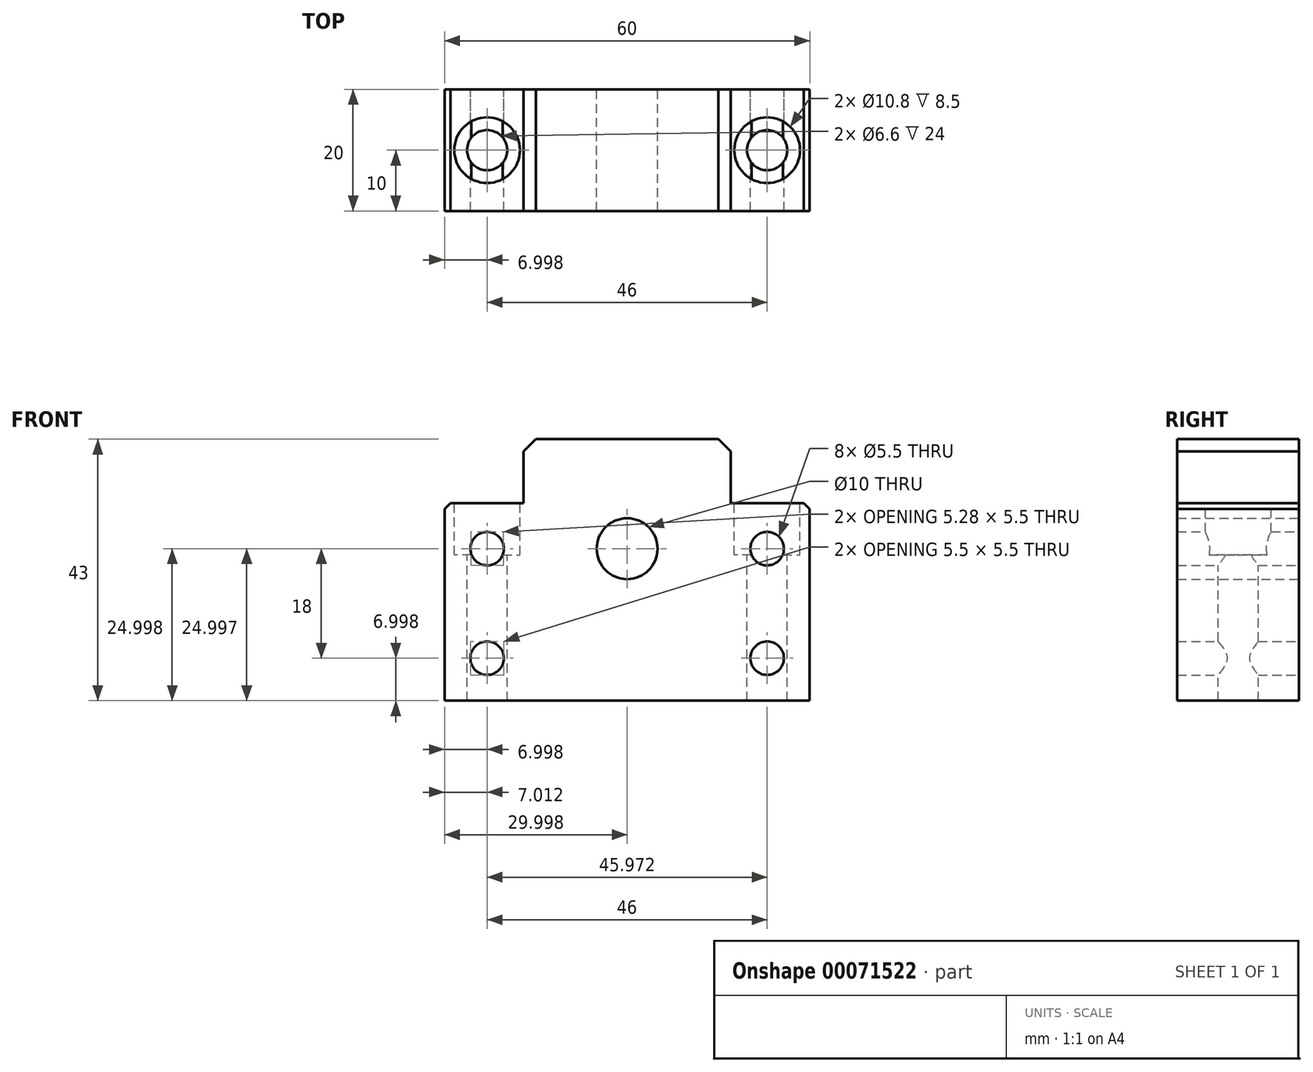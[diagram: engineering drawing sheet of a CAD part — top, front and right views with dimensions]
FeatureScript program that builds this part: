
annotation { "Feature Type Name" : "Feature", "Feature Type Description" : "" }
export const myFeature = defineFeature(function(context is Context, id is Id, definition is map)
    precondition{}
    {
        {
            var Q0;
            Q0=qCreatedBy(makeId("Front.planeOp"),FACE);
            var sketch = newSketch(context, id + "F0", { "sketchPlane" : qUnion([Q0])});
            skLineSegment(sketch, "E0.bottom", {"start": v(-44.44, 5.92) * mm, "end": v(-31.44, 5.92) * mm});
            skLineSegment(sketch, "E0.top", {"start": v(-44.44, -26.58) * mm, "end": v(15.56, -26.58) * mm});
            skLineSegment(sketch, "E0.left", {"start": v(-44.44, 5.92) * mm, "end": v(-44.44, -26.58) * mm});
            skLineSegment(sketch, "E0.right", {"start": v(15.56, 5.92) * mm, "end": v(15.56, -26.58) * mm});
            skLineSegment(sketch, "E1.bottom", {"start": v(-31.44, 16.42) * mm, "end": v(2.56, 16.42) * mm});
            skLineSegment(sketch, "E1.left", {"start": v(-31.44, 16.42) * mm, "end": v(-31.44, 5.92) * mm});
            skLineSegment(sketch, "E1.right", {"start": v(2.56, 16.42) * mm, "end": v(2.56, 5.92) * mm});
            skLineSegment(sketch, "E2.trimOffspring", {"start": v(2.56, 5.92) * mm, "end": v(15.56, 5.92) * mm});
            skCircle(sketch, "E3", {"center": v(-14.44, -1.58) * mm, "radius": 5 * mm});
            skCircle(sketch, "E4", {"center": v(-37.44, -1.58) * mm, "radius": 2.75 * mm});
            skCircle(sketch, "E5", {"center": v(-37.44, -19.58) * mm, "radius": 2.75 * mm});
            skCircle(sketch, "E6", {"center": v(8.56, -19.58) * mm, "radius": 2.75 * mm});
            skCircle(sketch, "E7", {"center": v(8.56, -1.58) * mm, "radius": 2.75 * mm});
            skSolve(sketch);
        }
        {
            var Q0;
            Q0=qSketchRegion(id+"F0",true);
            extrude(context, id + "F1", {"entities" : qUnion([Q0]), "depth" : 20 * mm});
        }
        {
            var Q0;
            Q0=makeQuery(id+"F1.opExtrude","SWEPT_EDGE",EDGE,{"disambiguationData":[OSD([sQuery(id+"F0.wireOp",EDGE,"E0.bottom"),sQuery(id+"F0.wireOp",EDGE,"E0.left")])]});
            var Q1;
            Q1=makeQuery(id+"F1.opExtrude","SWEPT_EDGE",EDGE,{"disambiguationData":[OSD([sQuery(id+"F0.wireOp",EDGE,"E0.right"),sQuery(id+"F0.wireOp",EDGE,"E2.trimOffspring")])]});
            chamfer(context, id + "F2", {"entities" : qUnion([Q0, Q1]), "width" : 1 * mm, "tangentPropagation" : true});
        }
        {
            var Q0;
            Q0=makeQuery(id+"F1.opExtrude","SWEPT_EDGE",EDGE,{"disambiguationData":[OSD([sQuery(id+"F0.wireOp",EDGE,"E1.bottom"),sQuery(id+"F0.wireOp",EDGE,"E1.left")])]});
            var Q1;
            Q1=makeQuery(id+"F1.opExtrude","SWEPT_EDGE",EDGE,{"disambiguationData":[OSD([sQuery(id+"F0.wireOp",EDGE,"E1.bottom"),sQuery(id+"F0.wireOp",EDGE,"E1.right")])]});
            chamfer(context, id + "F3", {"entities" : qUnion([Q0, Q1]), "width" : 2 * mm, "tangentPropagation" : true});
        }
        {
            var Q0;
            Q0=makeQuery(id+"F1.opExtrude","SWEPT_FACE",FACE,{"disambiguationData":[OSD([sQuery(id+"F0.wireOp",EDGE,"E0.bottom")])]});
            var sketch = newSketch(context, id + "F4", { "sketchPlane" : qUnion([Q0])});
            skCircle(sketch, "E8", {"center": v(-37.44, -10) * mm, "radius": 3.3 * mm});
            skCircle(sketch, "E9", {"center": v(8.56, -10) * mm, "radius": 3.3 * mm});
            skCircle(sketch, "E10", {"center": v(-37.44, -10) * mm, "radius": 5.4 * mm});
            skCircle(sketch, "E11", {"center": v(8.56, -10) * mm, "radius": 5.4 * mm});
            skSolve(sketch);
        }
        {
            var Q0;
            Q0=qSketchRegion(id+"F4",true);
            extrude(context, id + "F5", {"entities" : qUnion([Q0]), "operationType" : NewBodyOperationType.REMOVE, "oppositeDirection" : true, "depth" : 8.5 * mm});
        }
        {
            var Q0;
            Q0=makeQuery(id+"F4.imprint","IMPRINT",FACE,{"disambiguationData":[TD([[makeQuery(id+"F4.imprint","IMPRINT",EDGE,{"derivedFrom":sQuery(id+"F4.wireOp",EDGE,"E8")}),1.0]])]});
            var Q1;
            Q1=makeQuery(id+"F4.imprint","IMPRINT",FACE,{"disambiguationData":[TD([[makeQuery(id+"F4.imprint","IMPRINT",EDGE,{"derivedFrom":sQuery(id+"F4.wireOp",EDGE,"E9")}),1.0]])]});
            extrude(context, id + "F6", {"entities" : qUnion([Q0, Q1]), "operationType" : NewBodyOperationType.REMOVE, "endBound" : BoundingType.THROUGH_ALL, "oppositeDirection" : true, "depth" : 25 * mm});
        }
    });
